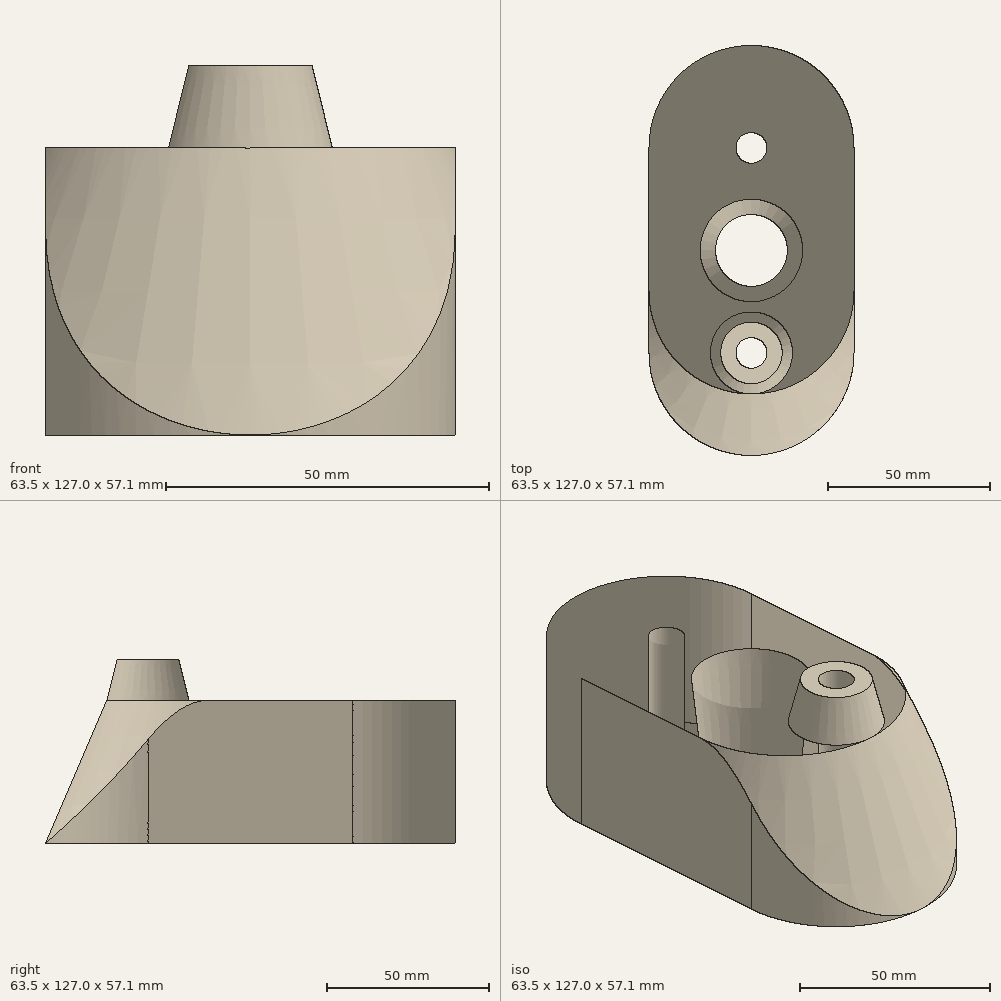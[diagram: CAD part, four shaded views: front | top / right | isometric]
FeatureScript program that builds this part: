
annotation { "Feature Type Name" : "Feature", "Feature Type Description" : "" }
export const myFeature = defineFeature(function(context is Context, id is Id, definition is map)
    precondition{}
    {
        {
            var Q0;
            Q0=qCreatedBy(makeId("Top.planeOp"),FACE);
            var sketch = newSketch(context, id + "F0", { "sketchPlane" : qUnion([Q0])});
            skArc(sketch, "E0", {"start": v(-31.75, 0) * mm, "mid": v(0, -31.75) * mm, "end": v(31.75, 0) * mm});
            skLineSegment(sketch, "E1", {"start": v(0, 0) * mm, "end": v(0, 63.5) * mm, "construction": true});
            skArc(sketch, "E2", {"start": v(31.75, 63.5) * mm, "mid": v(0, 95.25) * mm, "end": v(-31.75, 63.5) * mm});
            skLineSegment(sketch, "E3", {"start": v(-31.75, 0) * mm, "end": v(-31.75, 63.5) * mm});
            skLineSegment(sketch, "E4", {"start": v(31.75, 0) * mm, "end": v(31.75, 63.5) * mm});
            skSolve(sketch);
        }
        {
            var Q0;
            Q0=makeQuery(id+"F0.imprint","IMPRINT",FACE,{"disambiguationData":[TD([[makeQuery(id+"F0.imprint","IMPRINT",EDGE,{"derivedFrom":sQuery(id+"F0.wireOp",EDGE,"E0")}),1.0]])]});
            extrude(context, id + "F1", {"entities" : qUnion([Q0]), "depth" : 44.45 * mm, "offsetDistance" : 25.4 * mm});
        }
        {
            var Q0;
            Q0=qCreatedBy(makeId("Front.planeOp"),FACE);
            cPlane(context, id + "F2", {"entities" : qUnion([Q0]), "cplaneType" : CPlaneType.OFFSET, "offset" : 31.75 * mm, "oppositeDirection" : true, "width" : 152.4 * mm, "height" : 152.4 * mm});
        }
        {
            var Q0;
            Q0=qCreatedBy(makeId("Right.planeOp"),FACE);
            var sketch = newSketch(context, id + "F3", { "sketchPlane" : qUnion([Q0])});
            skLineSegment(sketch, "E5", {"start": v(-12.7, 44.45) * mm, "end": v(-31.75, 0) * mm});
            skLineSegment(sketch, "E6", {"start": v(-31.75, 0) * mm, "end": v(-31.75, 44.45) * mm});
            skLineSegment(sketch, "E7", {"start": v(-31.75, 44.45) * mm, "end": v(-12.7, 44.45) * mm});
            skLineSegment(sketch, "E8", {"start": v(19.05, 0) * mm, "end": v(19.05, 63.2) * mm, "construction": true});
            skSolve(sketch);
        }
        {
            var Q0;
            Q0 = qSketchRegion(id + "F3", true);
            var Q1;
            Q1=sQuery(id+"F3.wireOp",EDGE,"E8");
            revolve(context, id + "F4", {"operationType" : NewBodyOperationType.REMOVE, "surfaceOperationType" : NewSurfaceOperationType.NEW, "entities" : qUnion([Q0]), "axis" : qUnion([Q1]), "revolveType" : RevolveType.SYMMETRIC, "angle" : 180 * degree});
        }
        {
            var Q0;
            Q0=qCreatedBy(makeId("Right.planeOp"),FACE);
            var sketch = newSketch(context, id + "F5", { "sketchPlane" : qUnion([Q0])});
            skLineSegment(sketch, "E9", {"start": v(-12.7, 44.45) * mm, "end": v(-9.53, 57.15) * mm});
            skLineSegment(sketch, "E10", {"start": v(-9.53, 57.15) * mm, "end": v(0, 57.15) * mm});
            skLineSegment(sketch, "E11", {"start": v(0, 57.15) * mm, "end": v(0, 44.45) * mm});
            skLineSegment(sketch, "E12", {"start": v(0, 44.45) * mm, "end": v(-12.7, 44.45) * mm});
            skSolve(sketch);
        }
        {
            var Q0;
            Q0=makeQuery(id+"F5.imprint","IMPRINT",FACE,{"disambiguationData":[TD([[makeQuery(id+"F5.imprint","IMPRINT",EDGE,{"derivedFrom":sQuery(id+"F5.wireOp",EDGE,"E9")}),-1.0]])]});
            var Q1;
            Q1=sQuery(id+"F5.wireOp",EDGE,"E11");
            revolve(context, id + "F6", {"operationType" : NewBodyOperationType.ADD, "surfaceOperationType" : NewSurfaceOperationType.NEW, "entities" : qUnion([Q0]), "axis" : qUnion([Q1]), "revolveType" : RevolveType.FULL});
        }
        {
            var Q0;
            Q0=qCreatedBy(makeId("Right.planeOp"),FACE);
            var sketch = newSketch(context, id + "F7", { "sketchPlane" : qUnion([Q0])});
            skLineSegment(sketch, "E13", {"start": v(31.75, 0) * mm, "end": v(31.75, 44.45) * mm});
            skLineSegment(sketch, "E14", {"start": v(31.75, 44.45) * mm, "end": v(15.88, 44.45) * mm});
            skLineSegment(sketch, "E15", {"start": v(15.88, 44.45) * mm, "end": v(20.64, 0) * mm});
            skLineSegment(sketch, "E16", {"start": v(20.64, 0) * mm, "end": v(31.75, 0) * mm});
            skSolve(sketch);
        }
        {
            var Q0;
            Q0 = qSketchRegion(id + "F7", true);
            var Q1;
            Q1=sQuery(id+"F7.wireOp",EDGE,"E13");
            revolve(context, id + "F8", {"operationType" : NewBodyOperationType.REMOVE, "surfaceOperationType" : NewSurfaceOperationType.NEW, "entities" : qUnion([Q0]), "axis" : qUnion([Q1]), "revolveType" : RevolveType.FULL, "oppositeDirection" : true});
        }
        {
            var Q0;
            Q0=makeQuery(id+"F6.opRevolve","SWEPT_FACE",FACE,{"disambiguationData":[OSD([sQuery(id+"F5.wireOp",EDGE,"E10")])]});
            var sketch = newSketch(context, id + "F9", { "sketchPlane" : qUnion([Q0])});
            skPoint(sketch, "E17", {"position": v(0, 0) * mm});
            skPoint(sketch, "E18", {"position": v(0, 63.5) * mm});
            skSolve(sketch);
        }
        {
            var Q0;
            Q0=sQuery(id+"F9.wireOp",VERTEX,"E17");
            var Q1;
            Q1=sQuery(id+"F9.wireOp",VERTEX,"E18");
            var Q2;
            Q2=makeQuery(id+"F1.opExtrude","SWEPT_BODY",BODY,{"disambiguationData":[OSD([sQuery(id+"F0.wireOp",EDGE,"E0"),sQuery(id+"F0.wireOp",EDGE,"E2"),sQuery(id+"F0.wireOp",EDGE,"E3"),sQuery(id+"F0.wireOp",EDGE,"E4")])]});
            hole(context, id + "F10", {"style" : HoleStyle.SIMPLE, "endStyle" : HoleEndStyle.THROUGH, "holeDiameter" : 9.52 * mm, "majorDiameter" : 6.35 * mm, "isTappedThrough" : true, "tappedDepth" : 12.7 * mm, "tapClearance" : 3, "locations" : qUnion([Q0, Q1]), "scope" : qUnion([Q2])});
        }
    });
